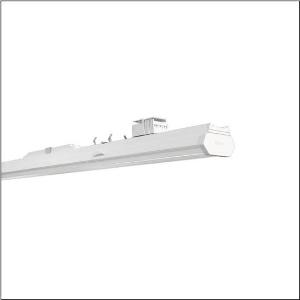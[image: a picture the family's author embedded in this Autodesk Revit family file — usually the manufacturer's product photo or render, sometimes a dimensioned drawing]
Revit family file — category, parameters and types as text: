
# Revit family: licross_r__11_protected_mo_51tp127n485g_ff31
name_source: partatom
category: Lighting Fixtures
units: mm (PartAtom-declared; Revit-internal decimal feet)

## family parameters
Cut with Voids When Loaded = No
Host = Face
Light Source = No
Part Type = Normal
Room Calculation Point = No
Round Connector Dimension = Use Diameter
Shared = No

## types (1)
- Licross® 11 Protected MO (1 x LED, 8720 lm, 48.6 W, 4000K)
    Apparent Load = 49 VA
    CIE Flux Codes = 73 92 98 99 100
    Color Rendering = 80
    Color Temperature = 4000K
    Default Elevation = 1800 mm
    Description = Licross® 11 Protected MO, luminaire insert, of sheet steel, galvanised, coil coated, white, length: 1.500mm, width: 90mm, height: 101mm, LED rated luminous flux: 8.720lm, light colour: 840, control gear: ON/OFF, with plug, 3-pole, with phase selection, mains connection: 220..240V, AC, 50/60Hz, rated input power: 49W, halogen-free wiring, primary light control with lens, of plastic, primary optical cover: cover, of PMMA, light emission: direct distribution, primary light characteristic: symmetric, protection rating (complete): IP64, insulation class (complete): insulation class I (protective earthing), certification: CE, ENEC, VDE, UKCA, protection symbol: D if used in an environment with conductive dust loads with corresponding accessories, impact resistance: IK06, permissible ambient temperature for indoor applications: -25..+35°C, corresponds to IFS (International Featured Standards) requirements for safety and quality in the food industry, reducing of maximum allowable ambient temperature of 5°C with ceiling mounting, LABS conformity tested according to VDMA 24364:2018-05, packaging unit: 1 piece
    Height = 92 mm
    Lamp = 1 x LED
    Lamp Light Flux = 8720 lm
    Lamp Power = 48.6 W
    Lamp count = 1
    Length = 1500 mm
    Luminous efficacy = 179 lm/W
    Manufacturer = Siteco
    ModVariant = No
    Model = 51TP127N485G
    Mounting Place = Ceiling
    Mounting Type = Pendant
    Number of Poles = 1
    OnlyDefault = Yes
    Power Factor = 1
    Product Name = Licross® 11 Protected MO
    Product group = luminaire insert
    ProductGroupID = 901
    Protection Class = Protection class I
    Protection Degree = IP 64
    RLX_Detail_Level = 1
    RLX_Emergency_Light_Flux = 0 lm
    RLX_Emergency_Type = 0
    RLX_Emergency_Type_DB = No
    RlxData = <blob elided: 20689 chars, md5=ac03c364>
    Socket = socket
    Standby Power = 0 W
    System Light Flux = 8720 lm
    System Power = 49 W
    Type Comments = Product without accessories
    Type Image = l_1256148.jpg
    URL = http://relux.com
    VarID = ---
    Voltage = 0 V
    Weight = 0.00 kg
    Width = 88 mm

## geometry (parser evidence)
native form markers: Blend x4, Sweep x13
no freeform markers — native parametric forms only
